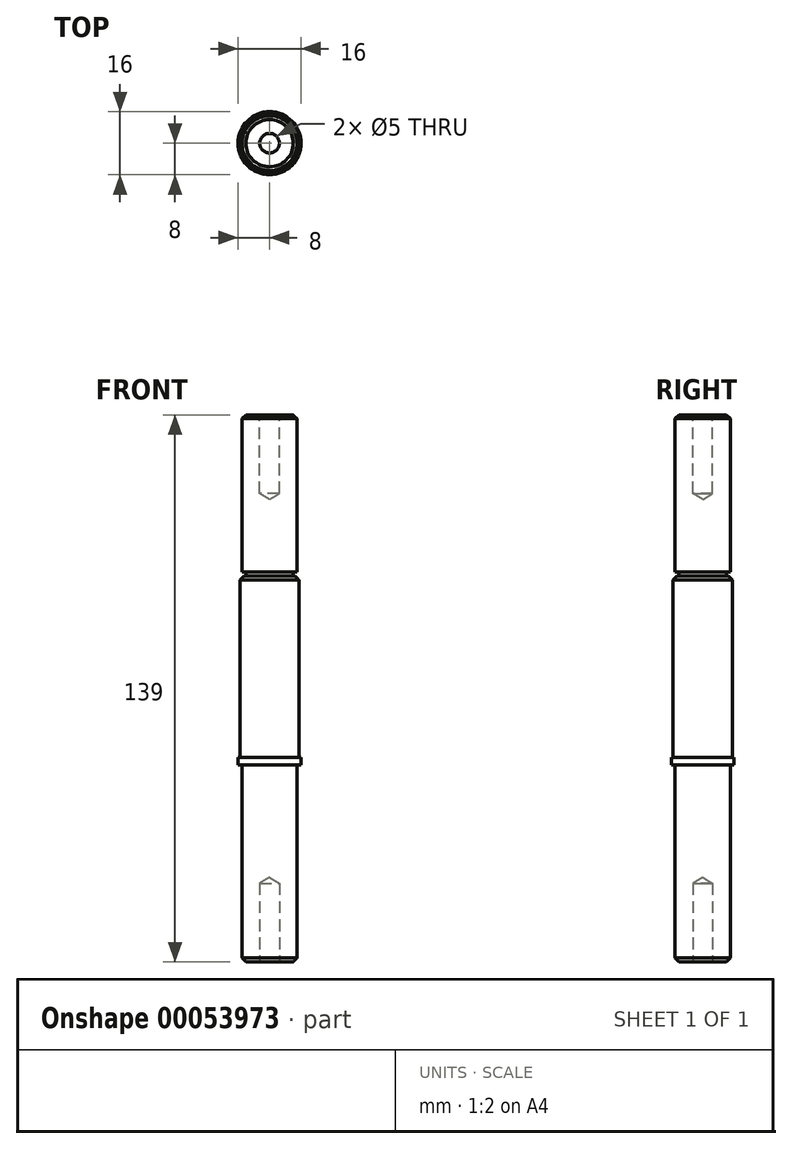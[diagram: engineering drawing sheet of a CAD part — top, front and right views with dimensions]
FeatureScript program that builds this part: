
annotation { "Feature Type Name" : "Feature", "Feature Type Description" : "" }
export const myFeature = defineFeature(function(context is Context, id is Id, definition is map)
    precondition{}
    {
        {
            var Q0;
            Q0=qCreatedBy(makeId("Top.planeOp"),FACE);
            var sketch = newSketch(context, id + "F0", { "sketchPlane" : qUnion([Q0])});
            skCircle(sketch, "E0", {"center": v(0, 0) * mm, "radius": 7 * mm});
            skSolve(sketch);
        }
        {
            var Q0;
            Q0 = qSketchRegion(id + "F0", true);
            extrude(context, id + "F1", {"entities" : qUnion([Q0]), "depth" : 50 * mm, "offsetDistance" : 25 * mm});
        }
        {
            var Q0;
            Q0=makeQuery(id+"F1.opExtrude","CAP_FACE",FACE,{"disambiguationData":[OSD([sQuery(id+"F0.wireOp",EDGE,"E0")])],"isStart":false});
            var sketch = newSketch(context, id + "F2", { "sketchPlane" : qUnion([Q0])});
            skCircle(sketch, "E1", {"center": v(0, 0) * mm, "radius": 8 * mm});
            skSolve(sketch);
        }
        {
            var Q0;
            Q0 = qSketchRegion(id + "F2", true);
            extrude(context, id + "F3", {"entities" : qUnion([Q0]), "operationType" : NewBodyOperationType.ADD, "depth" : 2 * mm, "offsetDistance" : 25 * mm});
        }
        {
            var Q0;
            Q0=makeQuery(id+"F3.opExtrude","CAP_FACE",FACE,{"disambiguationData":[OSD([sQuery(id+"F2.wireOp",EDGE,"E1")])],"isStart":false});
            var sketch = newSketch(context, id + "F4", { "sketchPlane" : qUnion([Q0])});
            skCircle(sketch, "E2", {"center": v(0, 0) * mm, "radius": 7.5 * mm});
            skSolve(sketch);
        }
        {
            var Q0;
            Q0 = qSketchRegion(id + "F4", true);
            extrude(context, id + "F5", {"entities" : qUnion([Q0]), "operationType" : NewBodyOperationType.ADD, "depth" : 46 * mm, "offsetDistance" : 25 * mm});
        }
        {
            var Q0;
            Q0=makeQuery(id+"F5.opExtrude","CAP_FACE",FACE,{"disambiguationData":[OSD([sQuery(id+"F4.wireOp",EDGE,"E2")])],"isStart":false});
            var sketch = newSketch(context, id + "F6", { "sketchPlane" : qUnion([Q0])});
            skCircle(sketch, "E3", {"center": v(0, 0) * mm, "radius": 6 * mm});
            skSolve(sketch);
        }
        {
            var Q0;
            Q0 = qSketchRegion(id + "F6", true);
            extrude(context, id + "F7", {"entities" : qUnion([Q0]), "operationType" : NewBodyOperationType.ADD, "depth" : 1 * mm, "offsetDistance" : 25 * mm});
        }
        {
            var Q0;
            Q0=makeQuery(id+"F7.opExtrude","CAP_FACE",FACE,{"disambiguationData":[OSD([sQuery(id+"F6.wireOp",EDGE,"E3")])],"isStart":false});
            var sketch = newSketch(context, id + "F8", { "sketchPlane" : qUnion([Q0])});
            skCircle(sketch, "E4", {"center": v(0, 0) * mm, "radius": 7 * mm});
            skSolve(sketch);
        }
        {
            var Q0;
            Q0 = qSketchRegion(id + "F8", true);
            extrude(context, id + "F9", {"entities" : qUnion([Q0]), "operationType" : NewBodyOperationType.ADD, "depth" : 40 * mm, "offsetDistance" : 25 * mm});
        }
        {
            var Q0;
            Q0=makeQuery(id+"F9.opExtrude","CAP_FACE",FACE,{"disambiguationData":[OSD([sQuery(id+"F8.wireOp",EDGE,"E4")])],"isStart":false});
            var sketch = newSketch(context, id + "F10", { "sketchPlane" : qUnion([Q0])});
            skPoint(sketch, "E5", {"position": v(0, 0) * mm});
            skSolve(sketch);
        }
        {
            var Q0;
            Q0=sQuery(id+"F10.wireOp",VERTEX,"E5");
            var Q1;
            Q1=makeQuery(id+"F1.opExtrude","SWEPT_BODY",BODY,{"disambiguationData":[OSD([sQuery(id+"F0.wireOp",EDGE,"E0")])]});
            hole(context, id + "F11", {"style" : HoleStyle.SIMPLE, "endStyle" : HoleEndStyle.BLIND, "standardTappedOrClearance" : lookupTablePath({ "standard" : "ISO", "engagement" : "75%", "pitch" : "1 mm", "size" : "M6", "type" : "Tapped" }), "standardBlindInLast" : lookupTablePath({ "standard" : "ISO", "engagement" : "75%", "pitch" : "1 mm", "size" : "M6", "type" : "Tapped" }), "holeDiameter" : 5 * mm, "majorDiameter" : 6 * mm, "showTappedDepth" : true, "holeDepth" : 20 * mm, "isTappedThrough" : true, "tappedDepth" : 17 * mm, "tapClearance" : 3, "locations" : qUnion([Q0]), "scope" : qUnion([Q1])});
        }
        {
            var Q0;
            Q0=makeQuery(id+"F1.opExtrude","CAP_FACE",FACE,{"disambiguationData":[OSD([sQuery(id+"F0.wireOp",EDGE,"E0")])],"isStart":true});
            var sketch = newSketch(context, id + "F12", { "sketchPlane" : qUnion([Q0])});
            skPoint(sketch, "E6", {"position": v(0, 0) * mm});
            skSolve(sketch);
        }
        {
            var Q0;
            Q0=sQuery(id+"F12.wireOp",VERTEX,"E6");
            var Q1;
            Q1=makeQuery(id+"F1.opExtrude","SWEPT_BODY",BODY,{"disambiguationData":[OSD([sQuery(id+"F0.wireOp",EDGE,"E0")])]});
            hole(context, id + "F13", {"style" : HoleStyle.SIMPLE, "endStyle" : HoleEndStyle.BLIND, "standardTappedOrClearance" : lookupTablePath({ "standard" : "ISO", "engagement" : "75%", "pitch" : "1 mm", "size" : "M6", "type" : "Tapped" }), "standardBlindInLast" : lookupTablePath({ "standard" : "ISO", "engagement" : "75%", "pitch" : "1 mm", "size" : "M6", "type" : "Tapped" }), "holeDiameter" : 5 * mm, "majorDiameter" : 6 * mm, "showTappedDepth" : true, "holeDepth" : 20 * mm, "isTappedThrough" : true, "tappedDepth" : 17 * mm, "tapClearance" : 3, "locations" : qUnion([Q0]), "scope" : qUnion([Q1])});
        }
        {
            var Q0;
            Q0=makeQuery(id+"F1.opExtrude","CAP_EDGE",EDGE,{"disambiguationData":[OSD([sQuery(id+"F0.wireOp",EDGE,"E0")])],"isStart":true});
            var Q1;
            Q1=makeQuery(id+"F9.opExtrude","CAP_EDGE",EDGE,{"disambiguationData":[OSD([sQuery(id+"F8.wireOp",EDGE,"E4")])],"isStart":false});
            var Q2;
            Q2=makeQuery(id+"F5.opExtrude","CAP_EDGE",EDGE,{"disambiguationData":[OSD([sQuery(id+"F4.wireOp",EDGE,"E2")])],"isStart":false});
            chamfer(context, id + "F14", {"entities" : qUnion([Q0, Q1, Q2]), "width" : 1 * mm, "tangentPropagation" : true});
        }
    });
